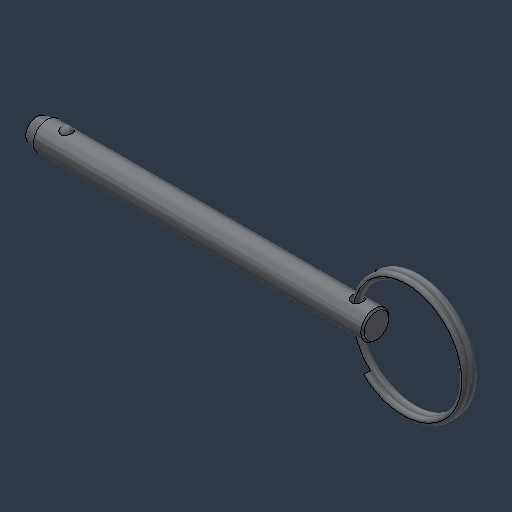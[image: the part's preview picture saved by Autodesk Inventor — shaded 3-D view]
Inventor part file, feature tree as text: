
AUTODESK INVENTOR PART (.ipt)
format: ipt  version: 2024.3 (Build 283343000, 343)  size: 217,600 bytes
history: native  units: mm (DEFAULTED — no unit token found)
features: revolve x1, other x1, sweep x1
ambient origin geometry x8: Origin, YZ Plane, XZ Plane, XY Plane, X Axis, Y Axis, Z Axis, Center Point
bodies: Solid1 (feature_tree), Solid2 (feature_tree), Solid3 (feature_tree)
feature tree (3):
  revolve  "Revolve2"  [1 undecoded]
  other  "Cut-Revolve2"
  sweep  "Sweep2"
note: 1 required parameter value undecoded (feature->parameter linkage not recoverable at this tier; creation-order binding heuristic only, values carry confidence <= 0.55)
